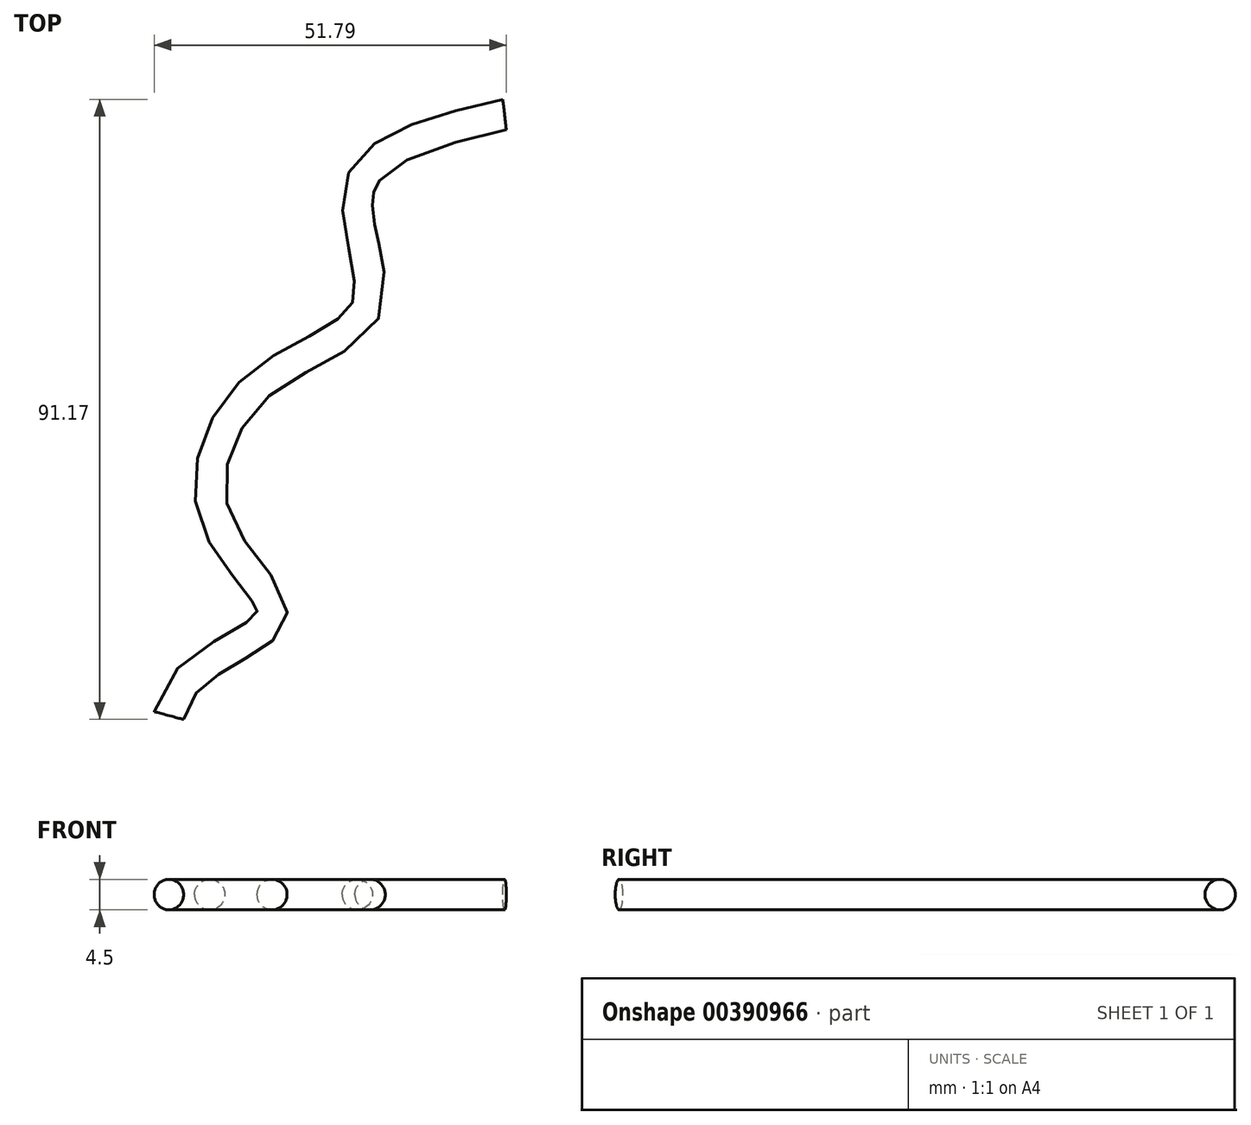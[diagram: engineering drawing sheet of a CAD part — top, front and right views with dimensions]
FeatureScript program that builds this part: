
annotation { "Feature Type Name" : "Feature", "Feature Type Description" : "" }
export const myFeature = defineFeature(function(context is Context, id is Id, definition is map)
    precondition{}
    {
        {
            var Q0;
            Q0=qCreatedBy(makeId("Top.planeOp"),FACE);
            var sketch = newSketch(context, id + "F0", { "sketchPlane" : qUnion([Q0])});
            skFitSpline(sketch, "E0", {"points": [v(0, 0) * mm, v(-21.3, -10.5) * mm, v(-20.15, -28.15) * mm, v(-36.07, -39.69) * mm, v(-42.3, -60.06) * mm, v(-34.4, -74.19) * mm, v(-49.35, -88.37) * mm], "startDerivative": vector(-159.76, -37.56) * mm, "endDerivative": vector(-21.07, -143.54) * mm});
            skLineSegment(sketch, "E1", {"start": v(-49.35, -88.37) * mm, "end": v(-45.11, -72.28) * mm, "construction": true});
            skSolve(sketch);
        }
        {
            var Q0;
            Q0=sQuery(id+"F0.wireOp",EDGE,"E1");
            var Q1;
            Q1=sQuery(id+"F0.wireOp",VERTEX,"E0.end");
            cPlane(context, id + "F1", {"entities" : qUnion([Q0, Q1]), "cplaneType" : CPlaneType.LINE_POINT, "offset" : 25.4 * mm, "width" : 152.4 * mm, "height" : 152.4 * mm});
        }
        {
            var Q0;
            Q0=qCreatedBy(id+"F1.planeOp",FACE);
            var sketch = newSketch(context, id + "F2", { "sketchPlane" : qUnion([Q0])});
            skCircle(sketch, "E2", {"center": v(25.19, 0) * mm, "radius": 2.25 * mm});
            skSolve(sketch);
        }
        {
            var Q0;
            Q0=makeQuery(id+"F2.imprint","IMPRINT",FACE,{"disambiguationData":[TD([[makeQuery(id+"F2.imprint","IMPRINT",EDGE,{"derivedFrom":sQuery(id+"F2.wireOp",EDGE,"E2")}),1.0]])]});
            var Q1;
            Q1=sQuery(id+"F0.wireOp",EDGE,"E0");
            sweep(context, id + "F3", {"profiles" : qUnion([Q0]), "path" : qUnion([Q1])});
        }
    });
